# Revit family: GP218-sw
name_source: partatom
category: Communication Devices
revit_build: Autodesk Revit Architecture 2012 (Build: 20110309_2315(x64)
units: mm (PartAtom-declared; Revit-internal decimal feet)

## types (1)
- GP218-sw
    Default Elevation = 48.000"
    Depth = 30.000"
    Description = Vented Dual 18" Subwoofer
    Enclosure Material = Black Finish
    Grill Depth = 1.250"
    Grill Extent Height = 17.625"
    Grill Material = Black Grille
    Grill Width = 45.750"
    Height = 20.000"
    Impedance = 4
    Manufacturer = QSC Audio Products, LLC
    Manufacturer URL = www.qscaudio.com
    Model = GP218-sw
    Power Handling = 4000
    Product Documentation Link = http://media.qscaudio.com
    Product Page URL = http://www.qscaudio.com
    Regulatory Compliance = RoHS
    SPL Max = 134.5
    Sensitivity = 134.5
    URL = http://www.qscaudio.com
    Weight Dimensional (kg) = 94.8
    Weight Dimensional (lb) = 209
    Weight Product (kg) = 86.6
    Weight Product (lb) = 191
    Width = 47.170"

## geometry (parser evidence)
native form markers: Sweep x1
no freeform markers — native parametric forms only
